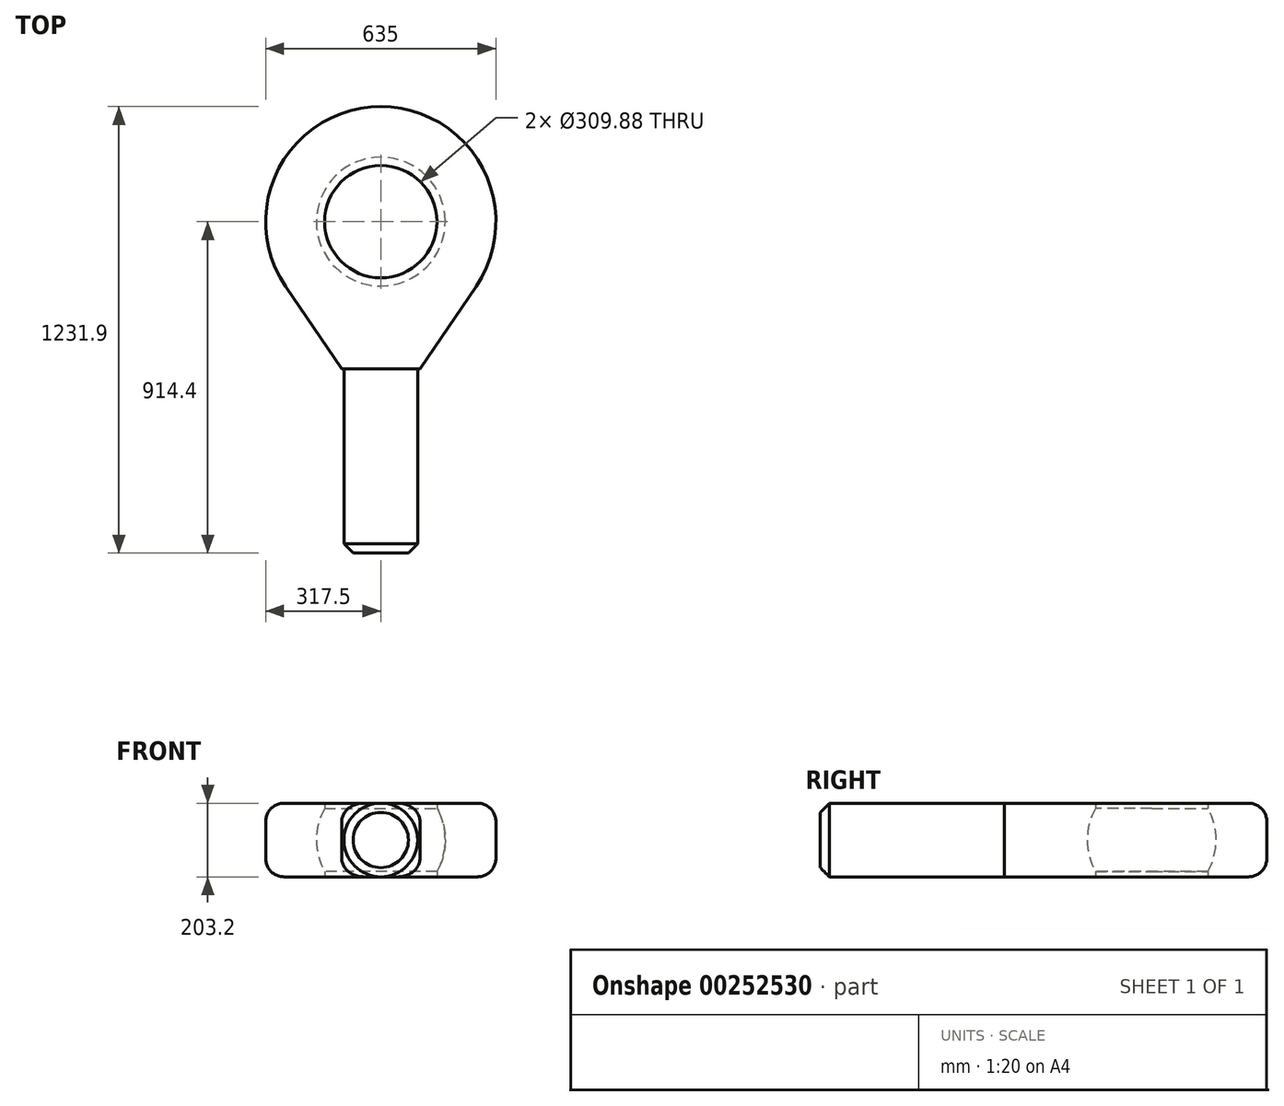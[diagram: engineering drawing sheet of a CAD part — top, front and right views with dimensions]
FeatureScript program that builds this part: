
annotation { "Feature Type Name" : "Feature", "Feature Type Description" : "" }
export const myFeature = defineFeature(function(context is Context, id is Id, definition is map)
    precondition{}
    {
        {
            var Q0;
            Q0=qCreatedBy(makeId("Top.planeOp"),FACE);
            var sketch = newSketch(context, id + "F0", { "sketchPlane" : qUnion([Q0])});
            skArc(sketch, "E0", {"start": v(262.74, -178.26) * mm, "mid": v(0, 317.5) * mm, "end": v(-262.74, -178.26) * mm});
            skCircle(sketch, "E1", {"center": v(0, 0) * mm, "radius": 154.94 * mm});
            skPoint(sketch, "E2", {"position": v(0, -406.4) * mm});
            skLineSegment(sketch, "E3", {"start": v(0, -406.4) * mm, "end": v(-107.95, -406.4) * mm});
            skLineSegment(sketch, "E4", {"start": v(107.95, -406.4) * mm, "end": v(0, -406.4) * mm});
            skLineSegment(sketch, "E5", {"start": v(-107.95, -406.4) * mm, "end": v(-262.74, -178.26) * mm});
            skLineSegment(sketch, "E6", {"start": v(262.74, -178.26) * mm, "end": v(107.95, -406.4) * mm});
            skSolve(sketch);
        }
        {
            var Q0;
            Q0=makeQuery(id+"F0.imprint","IMPRINT",FACE,{"disambiguationData":[TD([[makeQuery(id+"F0.imprint","IMPRINT",EDGE,{"derivedFrom":sQuery(id+"F0.wireOp",EDGE,"E0")}),1.0]])]});
            extrude(context, id + "F1", {"entities" : qUnion([Q0]), "depth" : 203.2 * mm});
        }
        {
            var Q0;
            Q0=makeQuery(id+"F1.opExtrude","SWEPT_FACE",FACE,{"disambiguationData":[OSD([sQuery(id+"F0.wireOp",EDGE,"E3"),sQuery(id+"F0.wireOp",EDGE,"E4")])]});
            var sketch = newSketch(context, id + "F2", { "sketchPlane" : qUnion([Q0])});
            skPoint(sketch, "E7", {"position": v(0, 203.2) * mm});
            skPoint(sketch, "E8", {"position": v(-107.95, 101.6) * mm});
            skPoint(sketch, "E9", {"position": v(0, 101.6) * mm});
            skCircle(sketch, "E10", {"center": v(0, 101.6) * mm, "radius": 101.6 * mm});
            skSolve(sketch);
        }
        {
            var Q0;
            {var subQ0=sQuery(id+"F2.wireOp",EDGE,"E10");var subQ1=sQuery(id+"F0.wireOp",EDGE,"E4");var subQ2=sQuery(id+"F0.wireOp",EDGE,"E3");var subQ3=makeQuery(id+"F2.imprint","INTERSECT",VERTEX,{"derivedFrom":[makeQuery(id+"F1.opExtrude","CAP_EDGE",EDGE,{"disambiguationData":[OSD([subQ2,subQ1])],"isStart":true}),subQ0]});Q0=makeQuery(id+"F2.imprint","IMPRINT",FACE,{"disambiguationData":[TD([[makeQuery(id+"F2.imprint","IMPRINT",EDGE,{"disambiguationData":[TD([[subQ3,1.0]])],"derivedFrom":subQ0}),1.0]])]});}
            extrude(context, id + "F3", {"entities" : qUnion([Q0]), "operationType" : NewBodyOperationType.ADD, "depth" : 508 * mm});
        }
        {
            var Q0;
            Q0=qCreatedBy(makeId("Right.planeOp"),FACE);
            var sketch = newSketch(context, id + "F4", { "sketchPlane" : qUnion([Q0])});
            skPoint(sketch, "E11", {"position": v(0, 101.6) * mm});
            skArc(sketch, "E12", {"start": v(-145.91, 203.2) * mm, "mid": v(-177.8, 101.6) * mm, "end": v(-145.91, 0) * mm});
            skPoint(sketch, "E13.orphan", {"position": v(0, 0) * mm});
            skPoint(sketch, "E14.end.orphan", {"position": v(0, 203.2) * mm});
            skLineSegment(sketch, "E15", {"start": v(-145.91, 0) * mm, "end": v(145.91, 0) * mm});
            skArc(sketch, "E16.trimOffspring", {"start": v(145.91, 0) * mm, "mid": v(177.8, 101.6) * mm, "end": v(145.91, 203.2) * mm});
            skLineSegment(sketch, "E17", {"start": v(-145.91, 203.2) * mm, "end": v(145.91, 203.2) * mm});
            skLineSegment(sketch, "E18", {"start": v(0, 203.2) * mm, "end": v(0, 0) * mm});
            skSolve(sketch);
        }
        {
            var Q0;
            {var subQ0=sQuery(id+"F4.wireOp",EDGE,"E12");Q0=makeQuery(id+"F4.imprint","IMPRINT",FACE,{"disambiguationData":[TD([[makeQuery(id+"F4.imprint","IMPRINT",EDGE,{"derivedFrom":subQ0}),1.0]])]});}
            var Q1;
            Q1=sQuery(id+"F4.wireOp",EDGE,"E18");
            revolve(context, id + "F5", {"operationType" : NewBodyOperationType.REMOVE, "entities" : qUnion([Q0]), "axis" : qUnion([Q1]), "revolveType" : RevolveType.FULL, "oppositeDirection" : true});
        }
        {
            var Q0;
            Q0=makeQuery(id+"F1.opExtrude","SWEPT_FACE",FACE,{"disambiguationData":[OSD([sQuery(id+"F0.wireOp",EDGE,"E0")])]});
            fillet(context, id + "F6", {"entities" : qUnion([Q0]), "radius" : 50.8 * mm, "tangentPropagation" : true, "allowEdgeOverflow" : false});
        }
        {
            var Q0;
            Q0=makeQuery(id+"F3.opExtrude","CAP_EDGE",EDGE,{"disambiguationData":[OSD([sQuery(id+"F2.wireOp",EDGE,"E10")])],"isStart":false});
            chamfer(context, id + "F7", {"entities" : qUnion([Q0]), "width" : 25.4 * mm, "tangentPropagation" : true});
        }
    });
